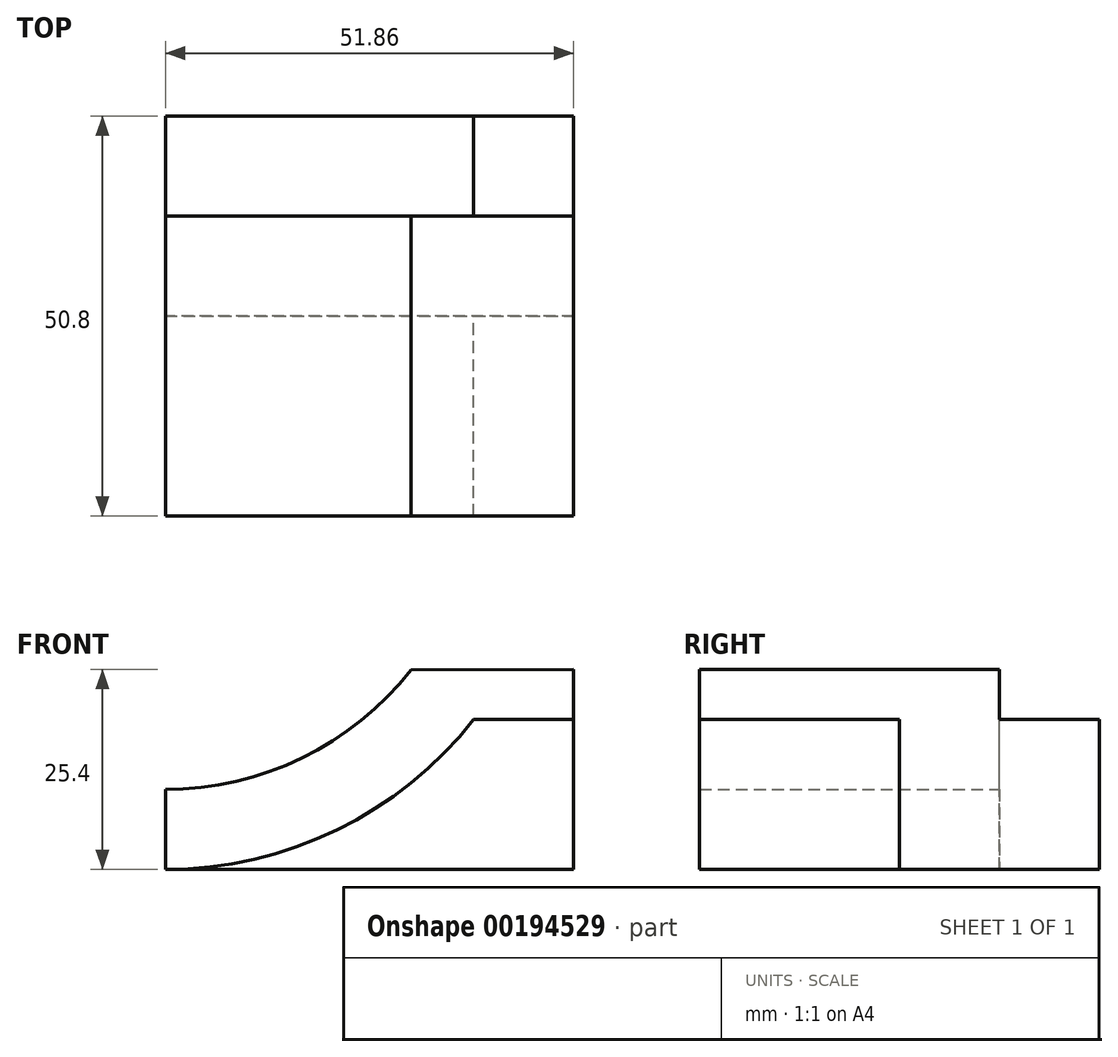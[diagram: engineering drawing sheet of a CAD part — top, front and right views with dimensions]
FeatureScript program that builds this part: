
annotation { "Feature Type Name" : "Feature", "Feature Type Description" : "" }
export const myFeature = defineFeature(function(context is Context, id is Id, definition is map)
    precondition{}
    {
        {
            var Q0;
            Q0=qCreatedBy(makeId("Front.planeOp"),FACE);
            var sketch = newSketch(context, id + "F0", { "sketchPlane" : qUnion([Q0])});
            skLineSegment(sketch, "E0.bottom", {"start": v(0, 0) * mm, "end": v(-63.5, 0) * mm});
            skLineSegment(sketch, "E0.top", {"start": v(0, -25.4) * mm, "end": v(-63.5, -25.4) * mm});
            skLineSegment(sketch, "E0.left", {"start": v(0, 0) * mm, "end": v(0, -25.4) * mm});
            skLineSegment(sketch, "E0.right", {"start": v(-63.5, 0) * mm, "end": v(-63.5, -25.4) * mm});
            skLineSegment(sketch, "E1.bottom", {"start": v(0, 0) * mm, "end": v(38.1, 0) * mm});
            skLineSegment(sketch, "E1.top", {"start": v(0, 25.4) * mm, "end": v(38.1, 25.4) * mm});
            skLineSegment(sketch, "E1.left", {"start": v(0, 0) * mm, "end": v(0, 25.4) * mm});
            skLineSegment(sketch, "E1.right", {"start": v(38.1, 0) * mm, "end": v(38.1, 25.4) * mm});
            skArc(sketch, "E2", {"start": v(38.1, 0) * mm, "mid": v(30.66, -17.96) * mm, "end": v(12.7, -25.4) * mm});
            skLineSegment(sketch, "E3", {"start": v(0, 25.4) * mm, "end": v(31.3, 25.4) * mm});
            skLineSegment(sketch, "E4", {"start": v(12.7, -25.4) * mm, "end": v(0, -25.4) * mm});
            skLineSegment(sketch, "E5.0", {"start": v(-12.7, 19.05) * mm, "end": v(0, 19.05) * mm});
            skArc(sketch, "E6.0", {"start": v(31.75, 0) * mm, "mid": v(26.17, -13.47) * mm, "end": v(12.7, -19.05) * mm});
            skLineSegment(sketch, "E7.0", {"start": v(12.7, -19.05) * mm, "end": v(0, -19.05) * mm});
            skLineSegment(sketch, "E8", {"start": v(-63.5, 0) * mm, "end": v(-51.86, 0) * mm});
            skArc(sketch, "E9", {"start": v(-51.86, 0) * mm, "mid": v(-30.09, 5.02) * mm, "end": v(-12.7, 19.05) * mm});
            skArc(sketch, "E10.0", {"start": v(-51.86, 10.16) * mm, "mid": v(-34.53, 14.15) * mm, "end": v(-20.7, 25.32) * mm});
            skLineSegment(sketch, "E11", {"start": v(-20.7, 25.32) * mm, "end": v(0, 25.4) * mm});
            skLineSegment(sketch, "E12", {"start": v(-51.86, 10.16) * mm, "end": v(-51.86, 0) * mm});
            skSolve(sketch);
        }
        {
            var Q0;
            {var subQ0=sQuery(id+"F0.wireOp",EDGE,"E0.bottom");Q0=makeQuery(id+"F0.imprint","IMPRINT",FACE,{"disambiguationData":[TD([[makeQuery(id+"F0.imprint","IMPRINT",EDGE,{"derivedFrom":subQ0}),-1.0]])]});}
            extrude(context, id + "F1", {"entities" : qUnion([Q0]), "endBound" : BoundingType.SYMMETRIC, "depth" : 25.4 * mm});
        }
        {
            var Q0;
            {var subQ0=sQuery(id+"F0.wireOp",EDGE,"E5.0");Q0=makeQuery(id+"F0.imprint","IMPRINT",FACE,{"disambiguationData":[TD([[makeQuery(id+"F0.imprint","IMPRINT",EDGE,{"derivedFrom":subQ0}),1.0]])]});}
            var Q1;
            {var subQ1=sQuery(id+"F0.wireOp",EDGE,"E2");Q1=makeQuery(id+"F0.imprint","IMPRINT",FACE,{"disambiguationData":[TD([[makeQuery(id+"F0.imprint","IMPRINT",EDGE,{"derivedFrom":subQ1}),-1.0]])]});}
            extrude(context, id + "F2", {"entities" : qUnion([Q0, Q1]), "operationType" : NewBodyOperationType.ADD, "depth" : 38.1 * mm});
        }
    });
